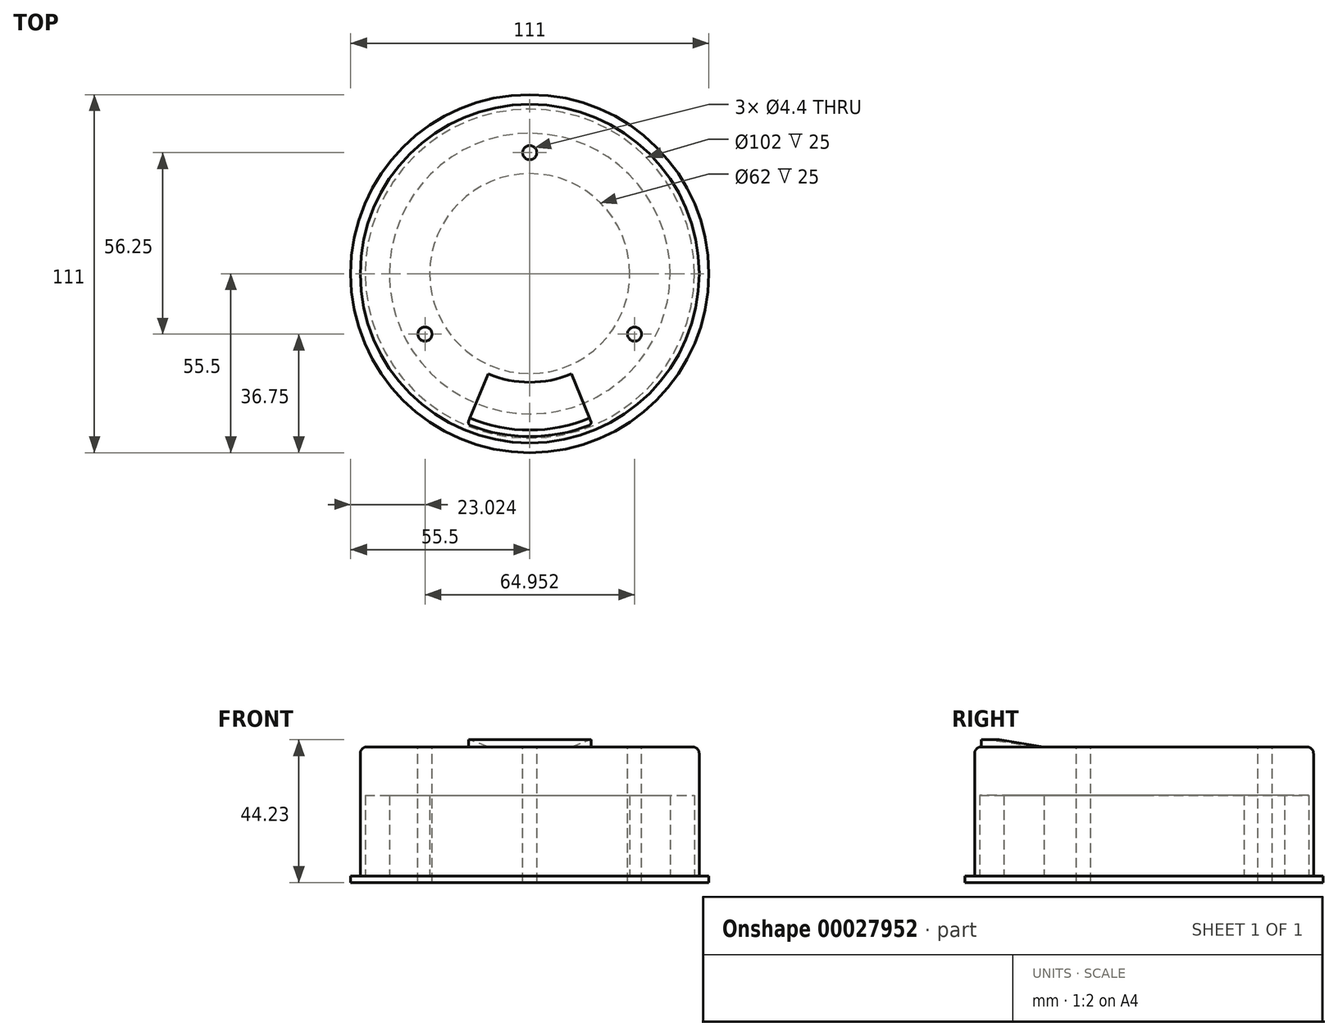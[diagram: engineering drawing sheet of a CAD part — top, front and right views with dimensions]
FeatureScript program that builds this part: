
annotation { "Feature Type Name" : "Feature", "Feature Type Description" : "" }
export const myFeature = defineFeature(function(context is Context, id is Id, definition is map)
    precondition{}
    {
        {
            var Q0;
            Q0=qCreatedBy(makeId("Top.planeOp"),FACE);
            var sketch = newSketch(context, id + "F0", { "sketchPlane" : qUnion([Q0])});
            skCircle(sketch, "E0", {"center": v(0, 0) * mm, "radius": 37.5 * mm});
            skLineSegment(sketch, "E1", {"start": v(0, 37.5) * mm, "end": v(-32.48, -18.75) * mm});
            skLineSegment(sketch, "E2", {"start": v(-32.48, -18.75) * mm, "end": v(32.48, -18.75) * mm});
            skLineSegment(sketch, "E3", {"start": v(32.48, -18.75) * mm, "end": v(0, 37.5) * mm});
            skLineSegment(sketch, "E4", {"start": v(0, -37.5) * mm, "end": v(-32.48, 18.75) * mm});
            skPoint(sketch, "E4.startSnap0", {"position": v(0, -18.75) * mm});
            skLineSegment(sketch, "E5", {"start": v(-32.48, 18.75) * mm, "end": v(32.48, 18.75) * mm});
            skLineSegment(sketch, "E6", {"start": v(32.48, 18.75) * mm, "end": v(0, -37.5) * mm});
            skSolve(sketch);
        }
        {
            var Q0;
            Q0=qCreatedBy(makeId("Top.planeOp"),FACE);
            var sketch = newSketch(context, id + "F1", { "sketchPlane" : qUnion([Q0])});
            skCircle(sketch, "E7", {"center": v(0, 0) * mm, "radius": 52.5 * mm});
            skSolve(sketch);
        }
        {
            var Q0;
            Q0=makeQuery(id+"F1.imprint","IMPRINT",FACE,{"disambiguationData":[TD([[makeQuery(id+"F1.imprint","IMPRINT",EDGE,{"derivedFrom":sQuery(id+"F1.wireOp",EDGE,"E7")}),1.0]])]});
            extrude(context, id + "F2", {"entities" : qUnion([Q0]), "oppositeDirection" : true, "depth" : 40 * mm});
        }
        {
            var Q0;
            Q0=qCreatedBy(makeId("Right.planeOp"),FACE);
            var sketch = newSketch(context, id + "F3", { "sketchPlane" : qUnion([Q0])});
            skLineSegment(sketch, "E8", {"start": v(-33.67, 0) * mm, "end": v(-48.5, 2.23) * mm});
            skLineSegment(sketch, "E9", {"start": v(-48.5, 2.23) * mm, "end": v(-50.5, 2.23) * mm});
            skLineSegment(sketch, "E10", {"start": v(-50.5, 2.23) * mm, "end": v(-50.5, 0) * mm});
            skLineSegment(sketch, "E11", {"start": v(-50.5, 0) * mm, "end": v(-33.67, 0) * mm});
            skLineSegment(sketch, "E12.bottom", {"start": v(0, 0) * mm, "end": v(-37.5, 0) * mm, "construction": true});
            skLineSegment(sketch, "E12.top", {"start": v(0, 25) * mm, "end": v(-37.5, 25) * mm, "construction": true});
            skLineSegment(sketch, "E12.left", {"start": v(0, 0) * mm, "end": v(0, 25) * mm, "construction": true});
            skLineSegment(sketch, "E12.right", {"start": v(-37.5, 0) * mm, "end": v(-37.5, 25) * mm, "construction": true});
            skLineSegment(sketch, "E13", {"start": v(-48.5, 2.23) * mm, "end": v(-44.92, 26.11) * mm, "construction": true});
            skLineSegment(sketch, "E14", {"start": v(-44.92, 26.11) * mm, "end": v(-30.08, 23.89) * mm, "construction": true});
            skLineSegment(sketch, "E15", {"start": v(-30.08, 23.89) * mm, "end": v(-33.67, 0) * mm, "construction": true});
            skLineSegment(sketch, "E16", {"start": v(52.5, 0) * mm, "end": v(52.5, -40) * mm, "construction": true});
            skLineSegment(sketch, "E17", {"start": v(-52.5, -40) * mm, "end": v(-52.5, 0) * mm, "construction": true});
            skLineSegment(sketch, "E18.bottom", {"start": v(-50.5, 2.23) * mm, "end": v(-48.5, 2.23) * mm});
            skLineSegment(sketch, "E18.top", {"start": v(-50.5, 4.23) * mm, "end": v(-48.5, 4.23) * mm});
            skLineSegment(sketch, "E18.left", {"start": v(-50.5, 2.23) * mm, "end": v(-50.5, 4.23) * mm});
            skLineSegment(sketch, "E18.right", {"start": v(-48.5, 2.23) * mm, "end": v(-48.5, 4.23) * mm});
            skSolve(sketch);
        }
        {
            var Q0;
            Q0=makeQuery(id+"F3.imprint","IMPRINT",FACE,{"disambiguationData":[TD([[makeQuery(id+"F3.imprint","IMPRINT",EDGE,{"derivedFrom":sQuery(id+"F3.wireOp",EDGE,"E8")}),1.0]])]});
            var Q1;
            Q1=makeQuery(id+"F3.imprint","IMPRINT",FACE,{"disambiguationData":[TD([[makeQuery(id+"F3.imprint","IMPRINT",EDGE,{"derivedFrom":sQuery(id+"F3.wireOp",EDGE,"E18.bottom")}),1.0]])]});
            var Q2;
            Q2=sQuery(id+"F3.wireOp",EDGE,"E12.left");
            revolve(context, id + "F4", {"operationType" : NewBodyOperationType.ADD, "entities" : qUnion([Q0, Q1]), "axis" : qUnion([Q2]), "revolveType" : RevolveType.SYMMETRIC, "angle" : 45 * degree});
        }
        {
            var Q0;
            Q0=makeQuery(id+"F2.opExtrude","CAP_EDGE",EDGE,{"disambiguationData":[OSD([sQuery(id+"F1.wireOp",EDGE,"E7")])],"isStart":true});
            fillet(context, id + "F5", {"entities" : qUnion([Q0]), "radius" : 2 * mm, "tangentPropagation" : true, "allowEdgeOverflow" : false});
        }
        {
            var Q0;
            Q0=makeQuery(id+"F2.opExtrude","CAP_FACE",FACE,{"disambiguationData":[OSD([sQuery(id+"F1.wireOp",EDGE,"E7")])],"isStart":false});
            var sketch = newSketch(context, id + "F6", { "sketchPlane" : qUnion([Q0])});
            skCircle(sketch, "E19", {"center": v(0, 0) * mm, "radius": 51 * mm});
            skSolve(sketch);
        }
        {
            var Q0;
            Q0=makeQuery(id+"F6.imprint","IMPRINT",FACE,{"disambiguationData":[TD([[makeQuery(id+"F6.imprint","IMPRINT",EDGE,{"derivedFrom":sQuery(id+"F6.wireOp",EDGE,"E19")}),1.0]])]});
            extrude(context, id + "F7", {"entities" : qUnion([Q0]), "operationType" : NewBodyOperationType.REMOVE, "oppositeDirection" : true, "depth" : 25 * mm});
        }
        {
            var Q0;
            Q0=makeQuery(id+"F2.opExtrude","CAP_FACE",FACE,{"disambiguationData":[OSD([sQuery(id+"F1.wireOp",EDGE,"E7")])],"isStart":false});
            var sketch = newSketch(context, id + "F8", { "sketchPlane" : qUnion([Q0])});
            skCircle(sketch, "E20", {"center": v(0, 0) * mm, "radius": 43.5 * mm});
            skCircle(sketch, "E21", {"center": v(0, 0) * mm, "radius": 31 * mm});
            skSolve(sketch);
        }
        {
            var Q0;
            Q0=makeQuery(id+"F8.imprint","IMPRINT",FACE,{"disambiguationData":[TD([[makeQuery(id+"F8.imprint","IMPRINT",EDGE,{"derivedFrom":sQuery(id+"F8.wireOp",EDGE,"E20")}),1.0]])]});
            extrude(context, id + "F9", {"entities" : qUnion([Q0]), "endBound" : BoundingType.UP_TO_NEXT, "oppositeDirection" : true, "depth" : 25 * mm});
        }
        {
            var Q0;
            Q0=makeQuery(id+"F9.opExtrude","CAP_FACE",FACE,{"disambiguationData":[OSD([sQuery(id+"F8.wireOp",EDGE,"E20"),sQuery(id+"F8.wireOp",EDGE,"E21")])],"isStart":true});
            var sketch = newSketch(context, id + "F10", { "sketchPlane" : qUnion([Q0])});
            skCircle(sketch, "E22", {"center": v(0, 0) * mm, "radius": 55.5 * mm});
            skSolve(sketch);
        }
        {
            var Q0;
            Q0=makeQuery(id+"F10.imprint","IMPRINT",FACE,{"disambiguationData":[TD([[makeQuery(id+"F10.imprint","IMPRINT",EDGE,{"derivedFrom":sQuery(id+"F10.wireOp",EDGE,"E22")}),1.0]])]});
            var Q1;
            Q1=makeQuery(id+"F10.imprint","IMPRINT",FACE,{"disambiguationData":[TD([[makeQuery(id+"F10.imprint","IMPRINT",EDGE,{"derivedFrom":makeQuery(id+"F9.opExtrude","CAP_EDGE",EDGE,{"disambiguationData":[OSD([sQuery(id+"F8.wireOp",EDGE,"E20")])],"isStart":true})}),1.0]])]});
            var Q2;
            Q2=makeQuery(id+"F10.imprint","IMPRINT",FACE,{"disambiguationData":[TD([[makeQuery(id+"F10.imprint","IMPRINT",EDGE,{"derivedFrom":makeQuery(id+"F9.opExtrude","CAP_EDGE",EDGE,{"disambiguationData":[OSD([sQuery(id+"F8.wireOp",EDGE,"E21")])],"isStart":true})}),1.0]])]});
            extrude(context, id + "F11", {"entities" : qUnion([Q0, Q1, Q2]), "operationType" : NewBodyOperationType.ADD, "depth" : 2 * mm});
        }
        {
            var Q0;
            Q0=makeQuery(id+"F2.opExtrude","CAP_FACE",FACE,{"disambiguationData":[OSD([sQuery(id+"F1.wireOp",EDGE,"E7")])],"isStart":true});
            var sketch = newSketch(context, id + "F12", { "sketchPlane" : qUnion([Q0])});
            skPoint(sketch, "E23", {"position": v(0, 37.5) * mm});
            skPoint(sketch, "E24", {"position": v(32.48, -18.75) * mm});
            skPoint(sketch, "E25", {"position": v(-32.48, -18.75) * mm});
            skCircle(sketch, "E26", {"center": v(0, 0) * mm, "radius": 37.5 * mm, "construction": true});
            skLineSegment(sketch, "E27", {"start": v(0, 37.5) * mm, "end": v(-32.48, -18.75) * mm, "construction": true});
            skLineSegment(sketch, "E28", {"start": v(32.48, -18.75) * mm, "end": v(0, 37.5) * mm, "construction": true});
            skLineSegment(sketch, "E29", {"start": v(32.48, -18.75) * mm, "end": v(-32.48, -18.75) * mm, "construction": true});
            skSolve(sketch);
        }
        {
            var Q0;
            Q0=sQuery(id+"F12.wireOp",VERTEX,"E23");
            var Q1;
            Q1=sQuery(id+"F12.wireOp",VERTEX,"E25");
            var Q2;
            Q2=sQuery(id+"F12.wireOp",VERTEX,"E24");
            var Q3;
            Q3=makeQuery(id+"F2.opExtrude","SWEPT_BODY",BODY,{"disambiguationData":[OSD([sQuery(id+"F1.wireOp",EDGE,"E7")])]});
            var Q4;
            Q4=makeQuery(id+"F9.opExtrude","SWEPT_BODY",BODY,{"disambiguationData":[OSD([sQuery(id+"F8.wireOp",EDGE,"E20"),sQuery(id+"F8.wireOp",EDGE,"E21")])]});
            hole(context, id + "F13", {"style" : HoleStyle.SIMPLE, "endStyle" : HoleEndStyle.THROUGH, "standardTappedOrClearance" : lookupTablePath({ "standard" : "ISO", "fit" : "Normal", "size" : "M4", "type" : "Clearance" }), "standardBlindInLast" : lookupTablePath({ "fit" : "Standard", "standard" : "ISO", "size" : "M4", "type" : "Clearance" }), "holeDiameter" : 4.4 * mm, "tappedDepth" : 12 * mm, "tapClearance" : 3, "locations" : qUnion([Q0, Q1, Q2]), "scope" : qUnion([Q3, Q4])});
        }
        {
            var Q0;
            Q0=makeQuery(id+"FCjLXsz7mxtYFee_1.1.F4.opRevolve","SWEPT_FACE",FACE,{"disambiguationData":[OSD([sQuery(id+"F3.wireOp",EDGE,"E18.top")])]});
            var Q1;
            Q1=makeQuery(id+"FCjLXsz7mxtYFee_1.2.F4.opRevolve","SWEPT_FACE",FACE,{"disambiguationData":[OSD([sQuery(id+"F3.wireOp",EDGE,"E18.top")])]});
            var Q2;
            Q2=makeQuery(id+"FCjLXsz7mxtYFee_1.1.F4.opRevolve","CAP_EDGE",EDGE,{"disambiguationData":[OSD([sQuery(id+"F3.wireOp",EDGE,"E10"),sQuery(id+"F3.wireOp",EDGE,"E18.left")])],"isStart":false});
            var Q3;
            Q3=makeQuery(id+"FCjLXsz7mxtYFee_1.2.F4.opRevolve","CAP_EDGE",EDGE,{"disambiguationData":[OSD([sQuery(id+"F3.wireOp",EDGE,"E10"),sQuery(id+"F3.wireOp",EDGE,"E18.left")])],"isStart":true});
            var Q4;
            Q4=makeQuery(id+"FCjLXsz7mxtYFee_1.2.F4.opRevolve","CAP_EDGE",EDGE,{"disambiguationData":[OSD([sQuery(id+"F3.wireOp",EDGE,"E10"),sQuery(id+"F3.wireOp",EDGE,"E18.left")])],"isStart":false});
            var Q5;
            Q5=makeQuery(id+"F4.opRevolve","CAP_EDGE",EDGE,{"disambiguationData":[OSD([sQuery(id+"F3.wireOp",EDGE,"E10"),sQuery(id+"F3.wireOp",EDGE,"E18.left")])],"isStart":true});
            var Q6;
            Q6=makeQuery(id+"F4.opRevolve","CAP_EDGE",EDGE,{"disambiguationData":[OSD([sQuery(id+"F3.wireOp",EDGE,"E10"),sQuery(id+"F3.wireOp",EDGE,"E18.left")])],"isStart":false});
            var Q7;
            Q7=makeQuery(id+"F4.opRevolve","SWEPT_FACE",FACE,{"disambiguationData":[OSD([sQuery(id+"F3.wireOp",EDGE,"E18.top")])]});
            var Q8;
            Q8=makeQuery(id+"FCjLXsz7mxtYFee_1.1.F4.opRevolve","CAP_EDGE",EDGE,{"disambiguationData":[OSD([sQuery(id+"F3.wireOp",EDGE,"E10"),sQuery(id+"F3.wireOp",EDGE,"E18.left")])],"isStart":true});
            fillet(context, id + "F14", {"entities" : qUnion([Q0, Q1, Q2, Q3, Q4, Q5, Q6, Q7, Q8]), "radius" : 1 * mm, "tangentPropagation" : true, "allowEdgeOverflow" : false});
        }
    });
